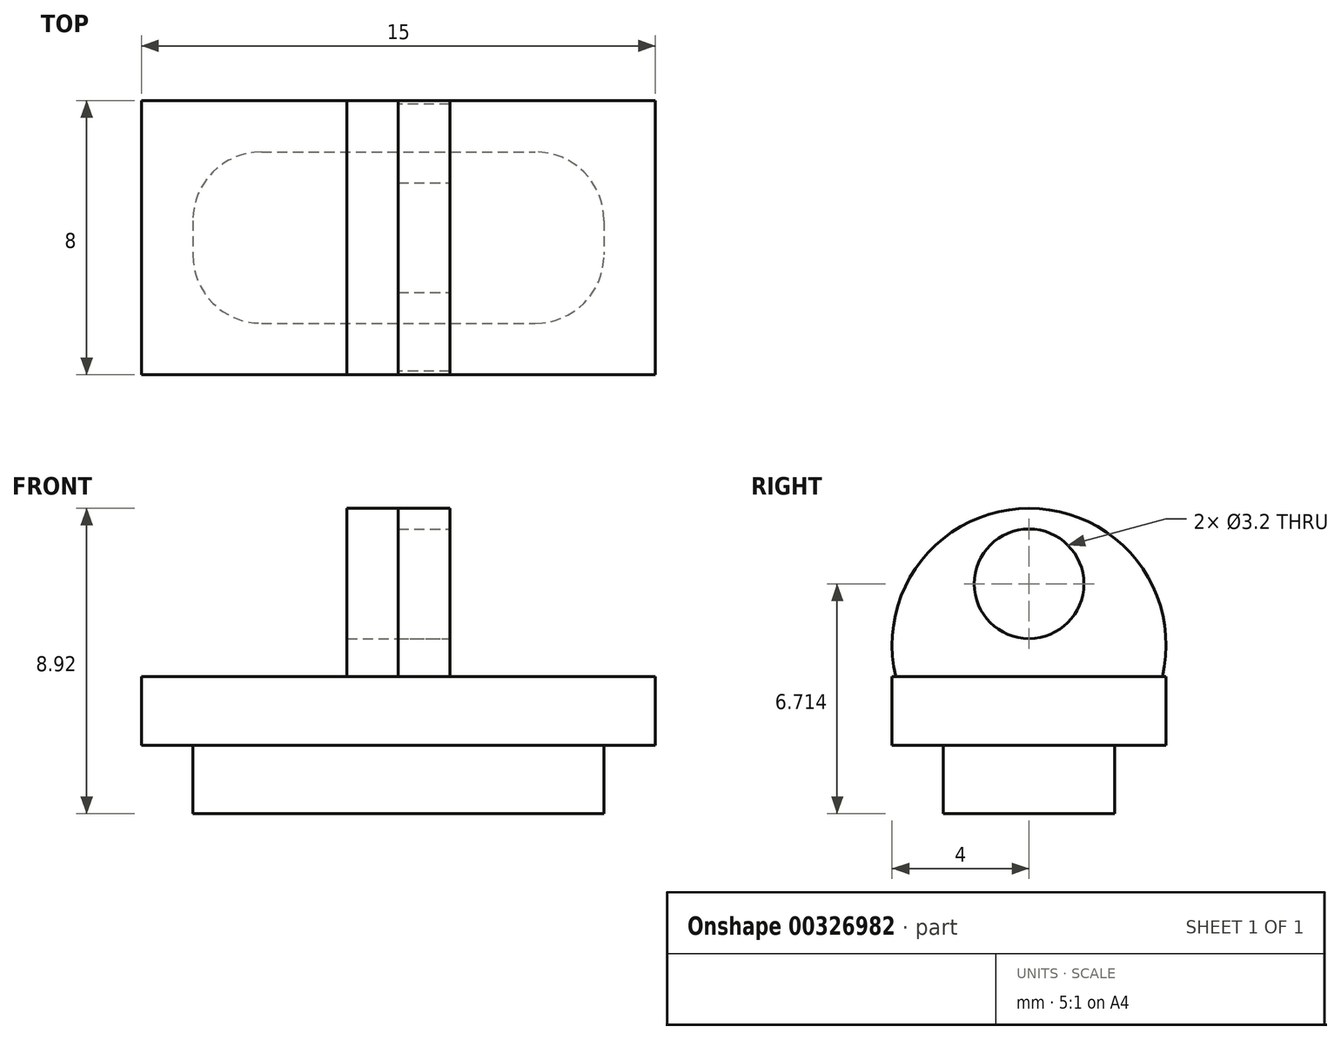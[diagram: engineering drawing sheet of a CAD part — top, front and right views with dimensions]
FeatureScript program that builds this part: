
annotation { "Feature Type Name" : "Feature", "Feature Type Description" : "" }
export const myFeature = defineFeature(function(context is Context, id is Id, definition is map)
    precondition{}
    {
        {
            var Q0;
            Q0=qCreatedBy(makeId("Top.planeOp"),FACE);
            var sketch = newSketch(context, id + "F0", { "sketchPlane" : qUnion([Q0])});
            skLineSegment(sketch, "E0.bottom", {"start": v(-6, 2.5) * mm, "end": v(6, 2.5) * mm});
            skLineSegment(sketch, "E0.top", {"start": v(-6, -2.5) * mm, "end": v(6, -2.5) * mm});
            skLineSegment(sketch, "E0.left", {"start": v(-6, 2.5) * mm, "end": v(-6, -2.5) * mm});
            skLineSegment(sketch, "E0.right", {"start": v(6, 2.5) * mm, "end": v(6, -2.5) * mm});
            skSolve(sketch);
        }
        {
            var Q0;
            Q0 = qSketchRegion(id + "F0", true);
            extrude(context, id + "F1", {"entities" : qUnion([Q0]), "oppositeDirection" : true, "depth" : 2 * mm});
        }
        {
            var Q0;
            Q0=makeQuery(id+"F1.opExtrude","SWEPT_EDGE",EDGE,{"disambiguationData":[OSD([sQuery(id+"F0.wireOp",EDGE,"E0.bottom"),sQuery(id+"F0.wireOp",EDGE,"E0.right")])]});
            var Q1;
            Q1=makeQuery(id+"F1.opExtrude","SWEPT_EDGE",EDGE,{"disambiguationData":[OSD([sQuery(id+"F0.wireOp",EDGE,"E0.top"),sQuery(id+"F0.wireOp",EDGE,"E0.right")])]});
            var Q2;
            Q2=makeQuery(id+"F1.opExtrude","SWEPT_EDGE",EDGE,{"disambiguationData":[OSD([sQuery(id+"F0.wireOp",EDGE,"E0.top"),sQuery(id+"F0.wireOp",EDGE,"E0.left")])]});
            var Q3;
            Q3=makeQuery(id+"F1.opExtrude","SWEPT_EDGE",EDGE,{"disambiguationData":[OSD([sQuery(id+"F0.wireOp",EDGE,"E0.bottom"),sQuery(id+"F0.wireOp",EDGE,"E0.left")])]});
            fillet(context, id + "F2", {"entities" : qUnion([Q0, Q1, Q2, Q3]), "radius" : 2 * mm, "tangentPropagation" : true, "allowEdgeOverflow" : false});
        }
        {
            var Q0;
            Q0=qCreatedBy(makeId("Top.planeOp"),FACE);
            var sketch = newSketch(context, id + "F3", { "sketchPlane" : qUnion([Q0])});
            skLineSegment(sketch, "E1.bottom", {"start": v(-7.5, 4) * mm, "end": v(7.5, 4) * mm});
            skLineSegment(sketch, "E1.top", {"start": v(-7.5, -4) * mm, "end": v(7.5, -4) * mm});
            skLineSegment(sketch, "E1.left", {"start": v(-7.5, 4) * mm, "end": v(-7.5, -4) * mm});
            skLineSegment(sketch, "E1.right", {"start": v(7.5, 4) * mm, "end": v(7.5, -4) * mm});
            skSolve(sketch);
        }
        {
            var Q0;
            Q0 = qSketchRegion(id + "F3", true);
            extrude(context, id + "F4", {"entities" : qUnion([Q0]), "operationType" : NewBodyOperationType.ADD, "depth" : 2 * mm});
        }
        {
            var Q0;
            Q0=qCreatedBy(makeId("Right.planeOp"),FACE);
            var sketch = newSketch(context, id + "F5", { "sketchPlane" : qUnion([Q0])});
            skArc(sketch, "E2", {"start": v(3.9, 2) * mm, "mid": v(0, 6.92) * mm, "end": v(-3.9, 2) * mm});
            skLineSegment(sketch, "E3", {"start": v(3.9, 2) * mm, "end": v(-3.9, 2) * mm});
            skSolve(sketch);
        }
        {
            var Q0;
            Q0 = qSketchRegion(id + "F5", true);
            extrude(context, id + "F6", {"entities" : qUnion([Q0]), "depth" : 1.5 * mm});
        }
        {
            var Q0;
            Q0 = qSketchRegion(id + "F5", true);
            extrude(context, id + "F7", {"entities" : qUnion([Q0]), "depth" : 1.5 * mm, "hasSecondDirection" : true, "secondDirectionOppositeDirection" : true, "secondDirectionDepth" : 1.5 * mm});
        }
        {
            var Q0;
            Q0=qCreatedBy(makeId("Right.planeOp"),FACE);
            var sketch = newSketch(context, id + "F8", { "sketchPlane" : qUnion([Q0])});
            skCircle(sketch, "E4", {"center": v(0, 4.71) * mm, "radius": 1.6 * mm});
            skSolve(sketch);
        }
        {
            var Q0;
            Q0 = qSketchRegion(id + "F8", true);
            extrude(context, id + "F9", {"entities" : qUnion([Q0]), "operationType" : NewBodyOperationType.REMOVE, "endBound" : BoundingType.UP_TO_NEXT, "oppositeDirection" : true, "depth" : 25 * mm, "hasSecondDirection" : true, "secondDirectionBound" : SecondDirectionBoundingType.UP_TO_NEXT, "secondDirectionOppositeDirection" : false, "secondDirectionDepth" : 25 * mm});
        }
    });
